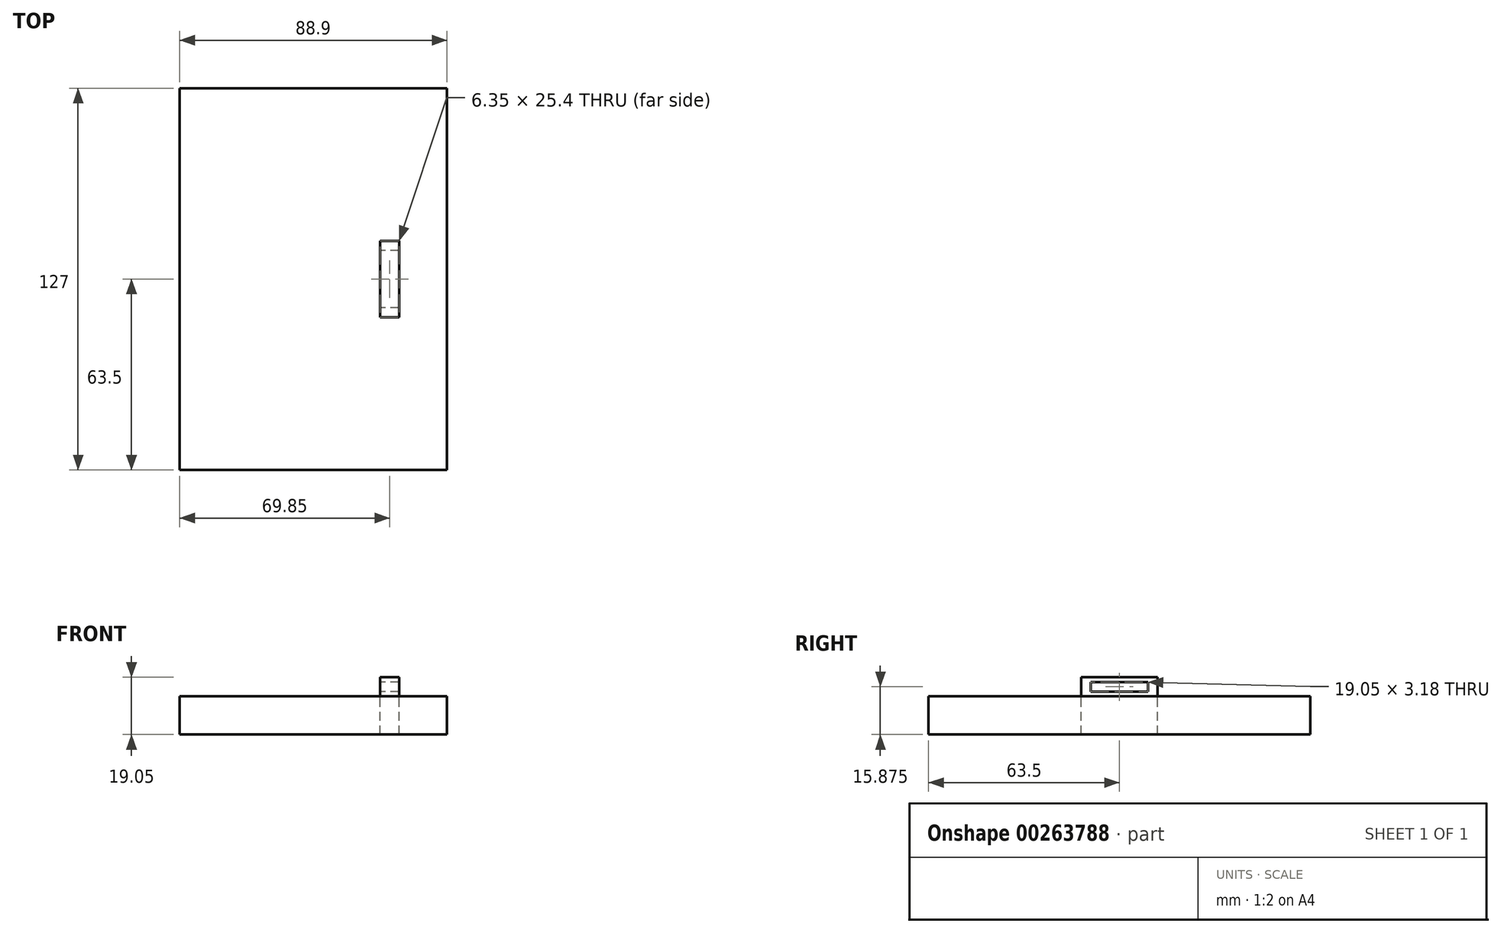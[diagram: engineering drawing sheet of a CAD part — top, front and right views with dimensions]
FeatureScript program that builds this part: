
annotation { "Feature Type Name" : "Feature", "Feature Type Description" : "" }
export const myFeature = defineFeature(function(context is Context, id is Id, definition is map)
    precondition{}
    {
        {
            var Q0;
            Q0=qCreatedBy(makeId("Top.planeOp"),FACE);
            var sketch = newSketch(context, id + "F0", { "sketchPlane" : qUnion([Q0])});
            skLineSegment(sketch, "E0.bottom", {"start": v(44.45, 63.5) * mm, "end": v(-44.45, 63.5) * mm});
            skLineSegment(sketch, "E0.top", {"start": v(44.45, -63.5) * mm, "end": v(-44.45, -63.5) * mm});
            skLineSegment(sketch, "E0.left", {"start": v(44.45, 63.5) * mm, "end": v(44.45, -63.5) * mm});
            skLineSegment(sketch, "E0.right", {"start": v(-44.45, 63.5) * mm, "end": v(-44.45, -63.5) * mm});
            skPoint(sketch, "E0.middle", {"position": v(0, 0) * mm});
            skLineSegment(sketch, "E1", {"start": v(0, 0) * mm, "end": v(25.4, 0) * mm});
            skLineSegment(sketch, "E2.bottom", {"start": v(28.58, -12.7) * mm, "end": v(22.23, -12.7) * mm});
            skLineSegment(sketch, "E2.top", {"start": v(28.58, 12.7) * mm, "end": v(22.22, 12.7) * mm});
            skLineSegment(sketch, "E2.left", {"start": v(28.58, -12.7) * mm, "end": v(28.57, 12.7) * mm});
            skLineSegment(sketch, "E2.right", {"start": v(22.23, -12.7) * mm, "end": v(22.22, 12.7) * mm});
            skPoint(sketch, "E2.middle", {"position": v(25.4, 0) * mm});
            skSolve(sketch);
        }
        {
            var Q0;
            Q0 = qSketchRegion(id + "F0", true);
            extrude(context, id + "F1", {"entities" : qUnion([Q0]), "oppositeDirection" : true, "depth" : 12.7 * mm});
        }
        {
            var Q0;
            {var subQ1=sQuery(id+"F0.wireOp",EDGE,"E2.bottom");Q0=makeQuery(id+"F0.imprint","IMPRINT",FACE,{"disambiguationData":[TD([[makeQuery(id+"F0.imprint","IMPRINT",EDGE,{"derivedFrom":subQ1}),-1.0]])]});}
            extrude(context, id + "F2", {"entities" : qUnion([Q0]), "depth" : 6.35 * mm});
        }
        {
            var Q0;
            Q0=makeQuery(id+"F2.opExtrude","SWEPT_FACE",FACE,{"disambiguationData":[OSD([sQuery(id+"F0.wireOp",EDGE,"E2.right")])]});
            var sketch = newSketch(context, id + "F3", { "sketchPlane" : qUnion([Q0])});
            skLineSegment(sketch, "E3", {"start": v(0, 0) * mm, "end": v(0, 3.18) * mm});
            skPoint(sketch, "E3.endSnap0", {"position": v(0, 6.35) * mm});
            skLineSegment(sketch, "E4.bottom", {"start": v(9.53, 4.76) * mm, "end": v(-9.52, 4.76) * mm});
            skLineSegment(sketch, "E4.top", {"start": v(9.53, 1.59) * mm, "end": v(-9.52, 1.59) * mm});
            skLineSegment(sketch, "E4.left", {"start": v(9.53, 4.76) * mm, "end": v(9.53, 1.59) * mm});
            skLineSegment(sketch, "E4.right", {"start": v(-9.52, 4.76) * mm, "end": v(-9.52, 1.59) * mm});
            skPoint(sketch, "E4.middle", {"position": v(0, 3.18) * mm});
            skSolve(sketch);
        }
        {
            var Q0;
            Q0 = qSketchRegion(id + "F3", true);
            extrude(context, id + "F4", {"entities" : qUnion([Q0]), "operationType" : NewBodyOperationType.REMOVE, "oppositeDirection" : true, "depth" : 25.4 * mm});
        }
    });
